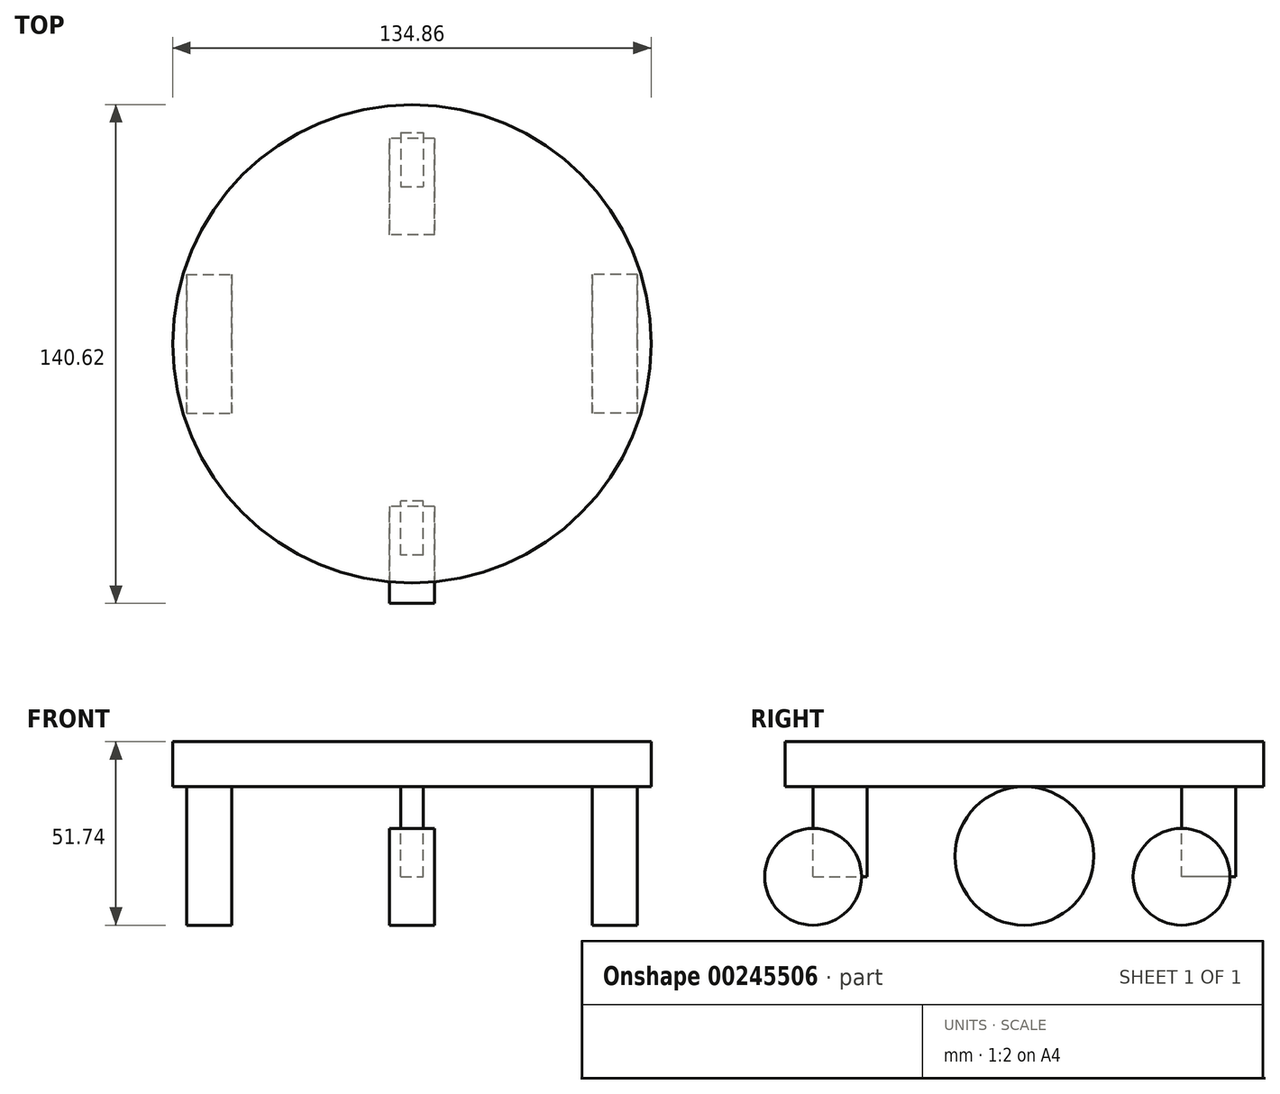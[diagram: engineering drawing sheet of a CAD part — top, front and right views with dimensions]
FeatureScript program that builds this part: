
annotation { "Feature Type Name" : "Feature", "Feature Type Description" : "" }
export const myFeature = defineFeature(function(context is Context, id is Id, definition is map)
    precondition{}
    {
        {
            var Q0;
            Q0=qCreatedBy(makeId("Top.planeOp"),FACE);
            var sketch = newSketch(context, id + "F0", { "sketchPlane" : qUnion([Q0])});
            skCircle(sketch, "E0", {"center": v(0, 0) * mm, "radius": 67.43 * mm});
            skLineSegment(sketch, "E1.bottom", {"start": v(-3.16, 59.55) * mm, "end": v(0, 59.55) * mm});
            skLineSegment(sketch, "E1.top", {"start": v(-3.16, 44.3) * mm, "end": v(0, 44.3) * mm});
            skLineSegment(sketch, "E1.left", {"start": v(-3.16, 59.55) * mm, "end": v(-3.16, 44.3) * mm});
            skLineSegment(sketch, "E2", {"start": v(0, 0) * mm, "end": v(95.1, 0) * mm, "construction": true});
            skLineSegment(sketch, "E3", {"start": v(0, 0) * mm, "end": v(0, 82.25) * mm, "construction": true});
            skLineSegment(sketch, "E4.MirrorCS", {"start": v(3.16, 59.55) * mm, "end": v(3.16, 44.3) * mm});
            skLineSegment(sketch, "E5.MirrorCS", {"start": v(3.16, 59.55) * mm, "end": v(0, 59.55) * mm});
            skLineSegment(sketch, "E6.MirrorCS", {"start": v(3.16, 44.3) * mm, "end": v(0, 44.3) * mm});
            skLineSegment(sketch, "E7.MirrorCS", {"start": v(3.16, -59.55) * mm, "end": v(3.16, -44.3) * mm});
            skLineSegment(sketch, "E8.MirrorCS", {"start": v(3.16, -59.55) * mm, "end": v(0, -59.55) * mm});
            skLineSegment(sketch, "E9.MirrorCS", {"start": v(-3.16, -59.55) * mm, "end": v(0, -59.55) * mm});
            skLineSegment(sketch, "E10.MirrorCS", {"start": v(-3.16, -59.55) * mm, "end": v(-3.16, -44.3) * mm});
            skLineSegment(sketch, "E11.MirrorCS", {"start": v(-3.16, -44.3) * mm, "end": v(0, -44.3) * mm});
            skLineSegment(sketch, "E12.MirrorCS", {"start": v(3.16, -44.3) * mm, "end": v(0, -44.3) * mm});
            skSolve(sketch);
        }
        {
            var Q0;
            Q0=makeQuery(id+"F0.imprint","IMPRINT",FACE,{"disambiguationData":[TD([[makeQuery(id+"F0.imprint","IMPRINT",EDGE,{"derivedFrom":sQuery(id+"F0.wireOp",EDGE,"E0")}),1.0]])]});
            var Q1;
            Q1=makeQuery(id+"F0.imprint","IMPRINT",FACE,{"disambiguationData":[TD([[makeQuery(id+"F0.imprint","IMPRINT",EDGE,{"derivedFrom":sQuery(id+"F0.wireOp",EDGE,"E1.bottom")}),-1.0]])]});
            var Q2;
            Q2=makeQuery(id+"F0.imprint","IMPRINT",FACE,{"disambiguationData":[TD([[makeQuery(id+"F0.imprint","IMPRINT",EDGE,{"derivedFrom":sQuery(id+"F0.wireOp",EDGE,"E7.MirrorCS")}),1.0]])]});
            extrude(context, id + "F1", {"entities" : qUnion([Q0, Q1, Q2]), "depth" : 12.7 * mm});
        }
        {
            var Q0;
            Q0=makeQuery(id+"F0.imprint","IMPRINT",FACE,{"disambiguationData":[TD([[makeQuery(id+"F0.imprint","IMPRINT",EDGE,{"derivedFrom":sQuery(id+"F0.wireOp",EDGE,"E7.MirrorCS")}),1.0]])]});
            var Q1;
            Q1=makeQuery(id+"F0.imprint","IMPRINT",FACE,{"disambiguationData":[TD([[makeQuery(id+"F0.imprint","IMPRINT",EDGE,{"derivedFrom":sQuery(id+"F0.wireOp",EDGE,"E1.bottom")}),-1.0]])]});
            extrude(context, id + "F2", {"entities" : qUnion([Q0, Q1]), "operationType" : NewBodyOperationType.ADD, "oppositeDirection" : true, "depth" : 25.4 * mm});
        }
        {
            var Q0;
            Q0=qCreatedBy(makeId("Right.planeOp"),FACE);
            var sketch = newSketch(context, id + "F3", { "sketchPlane" : qUnion([Q0])});
            skLineSegment(sketch, "E13", {"start": v(66.74, -39.04) * mm, "end": v(-72.77, -39.04) * mm, "construction": true});
            skLineSegment(sketch, "E14", {"start": v(0, 0) * mm, "end": v(0, -39.04) * mm, "construction": true});
            skCircle(sketch, "E15", {"center": v(0, -19.52) * mm, "radius": 19.52 * mm});
            skCircle(sketch, "E16", {"center": v(-59.55, -25.4) * mm, "radius": 13.64 * mm});
            skCircle(sketch, "E17", {"center": v(44.3, -25.4) * mm, "radius": 13.64 * mm});
            skSolve(sketch);
        }
        {
            var Q0;
            Q0=makeQuery(id+"F3.imprint","IMPRINT",FACE,{"disambiguationData":[TD([[makeQuery(id+"F3.imprint","IMPRINT",EDGE,{"derivedFrom":sQuery(id+"F3.wireOp",EDGE,"E15")}),1.0]])]});
            var Q1;
            Q1=sQuery(id+"F3.wireOp",EDGE,"E15");
            extrude(context, id + "F4", {"entities" : qUnion([Q0]), "operationType" : NewBodyOperationType.ADD, "surfaceEntities" : qUnion([Q1]), "depth" : 63.5 * mm, "hasSecondDirection" : true, "secondDirectionOppositeDirection" : false, "secondDirectionDepth" : 50.8 * mm});
        }
        {
            var Q0;
            Q0=makeQuery(id+"F3.imprint","IMPRINT",FACE,{"disambiguationData":[TD([[makeQuery(id+"F3.imprint","IMPRINT",EDGE,{"derivedFrom":sQuery(id+"F3.wireOp",EDGE,"E15")}),1.0]])]});
            extrude(context, id + "F5", {"entities" : qUnion([Q0]), "operationType" : NewBodyOperationType.ADD, "oppositeDirection" : true, "depth" : 63.5 * mm, "hasSecondDirection" : true, "secondDirectionOppositeDirection" : true, "secondDirectionDepth" : 50.8 * mm});
        }
        {
            var Q0;
            Q0=makeQuery(id+"F3.imprint","IMPRINT",FACE,{"disambiguationData":[TD([[makeQuery(id+"F3.imprint","IMPRINT",EDGE,{"derivedFrom":sQuery(id+"F3.wireOp",EDGE,"E16")}),1.0]])]});
            var Q1;
            Q1=makeQuery(id+"F3.imprint","IMPRINT",FACE,{"disambiguationData":[TD([[makeQuery(id+"F3.imprint","IMPRINT",EDGE,{"derivedFrom":sQuery(id+"F3.wireOp",EDGE,"E17")}),1.0]])]});
            extrude(context, id + "F6", {"entities" : qUnion([Q0, Q1]), "depth" : 6.35 * mm, "hasSecondDirection" : true, "secondDirectionOppositeDirection" : true, "secondDirectionDepth" : 6.35 * mm});
        }
    });
